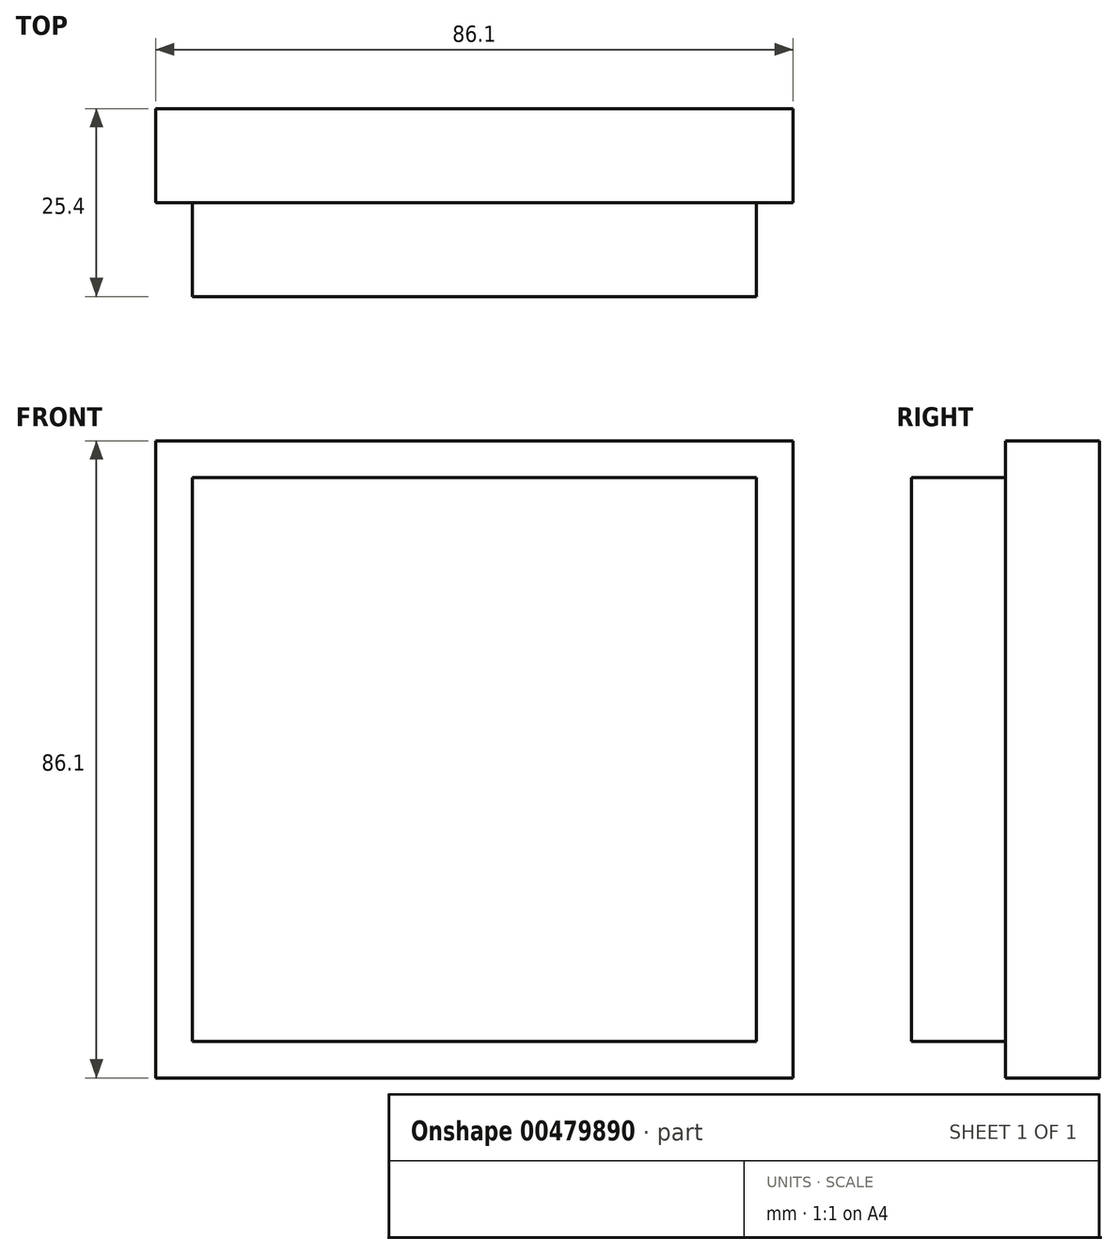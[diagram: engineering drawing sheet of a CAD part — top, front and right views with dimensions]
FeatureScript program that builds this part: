
annotation { "Feature Type Name" : "Feature", "Feature Type Description" : "" }
export const myFeature = defineFeature(function(context is Context, id is Id, definition is map)
    precondition{}
    {
        {
            var Q0;
            Q0=qCreatedBy(makeId("Front.planeOp"),FACE);
            var sketch = newSketch(context, id + "F0", { "sketchPlane" : qUnion([Q0])});
            skLineSegment(sketch, "E0.bottom", {"start": v(-44.45, 51.17) * mm, "end": v(31.75, 51.17) * mm});
            skLineSegment(sketch, "E0.top", {"start": v(-44.45, -25.03) * mm, "end": v(31.75, -25.03) * mm});
            skLineSegment(sketch, "E0.left", {"start": v(-44.45, 51.17) * mm, "end": v(-44.45, -25.03) * mm});
            skLineSegment(sketch, "E0.right", {"start": v(31.75, 51.17) * mm, "end": v(31.75, -25.03) * mm});
            skLineSegment(sketch, "E1.0", {"start": v(-49.4, 56.12) * mm, "end": v(36.7, 56.12) * mm});
            skLineSegment(sketch, "E1.1", {"start": v(-49.4, 56.12) * mm, "end": v(-49.4, -29.98) * mm});
            skLineSegment(sketch, "E1.2", {"start": v(-49.4, -29.98) * mm, "end": v(36.7, -29.98) * mm});
            skLineSegment(sketch, "E1.3", {"start": v(36.7, 56.12) * mm, "end": v(36.7, -29.98) * mm});
            skSolve(sketch);
        }
        {
            var Q0;
            Q0=makeQuery(id+"F0.imprint","IMPRINT",FACE,{"disambiguationData":[TD([[makeQuery(id+"F0.imprint","IMPRINT",EDGE,{"derivedFrom":sQuery(id+"F0.wireOp",EDGE,"E0.bottom")}),-1.0]])]});
            extrude(context, id + "F1", {"entities" : qUnion([Q0]), "depth" : 25.4 * mm});
        }
        {
            var Q0;
            Q0 = qSketchRegion(id + "F0", true);
            extrude(context, id + "F2", {"entities" : qUnion([Q0]), "operationType" : NewBodyOperationType.ADD, "depth" : 12.7 * mm});
        }
    });
